# Revit family: B&W_LS9086WW
name_source: partatom
category: Luminarias
units: mm (PartAtom-declared; Revit-internal decimal feet)

## family parameters
Compartido = No
Corte con vacíos al cargar = No
Cota de conector redondo = Diámetro de uso
Origen de luz = Sí
Punto de cálculo de habitación = No
Se basa en plano de trabajo = Sí
Siempre vertical = Sí
Tipo de pieza = Normal

## types (1)
- B&W_LS9086WW
    Cambio de temperatura de color de luz atenuada = <Ninguno>
    Comentarios de vataje = 127V
    Descripción = LUMINARIA TIPO CIRCULAR PARA EMPOTRAR EN TECHO CON CUERPO DE ALEACION EN ALUMINIO ACABADO EN COLOR BLANCO, IP 20 USO PARA INTERIORES CON CUERPO DE 0.4KG, CUENTA CON 1 LED TIPO SHARP CON UNA POTENCIA TOTAL DE 7W, A UNA TEMPERATURA EN BLANCO CALIDO 3000K CON 378LUMENES, EFICIENCIA DE 54LM/W, IRC 80, APERTURA A 30 GRADOS EN STOCK, 350mA EN CORRIENTE DE OPERACIÓN, ALIMENTADO A 127V. OPCION CON FUENTE ATENUABLE (NO INCLUIDA).
    Elevación por defecto = 1219 mm
    Fabricante = BRILLANT
    Filtro de color = 16777215
    Longitud de símbolo de origen de luz = 500 mm  [stored 1.64042 ft]
    Lámpara = SHARP
    Modelo = LS9086WW
    Watt per fixture = 7
    Ángulo de campo de foco = 30.00°
    Ángulo de enfoque = 30.00°
    Ángulo de inclinación = 60.00°

note: [stored X ft] marks values corroborated as IEEE doubles in the binary element streams (Revit-internal decimal feet)

## geometry (parser evidence)
native form markers: Blend x2
no freeform markers — native parametric forms only
